# Revit family: Faucet-Symmons-Duro-Lavatory_Pop_Up_Drain
name_source: partatom
category: Plumbing Fixtures
revit_build: Autodesk Revit 2015 (Build: 20140606_1530(x64)
units: mm (PartAtom-declared; Revit-internal decimal feet)

## types (4) — shared parameters
Date Modified = January 30, 2015
Equipment Abbreviation = LF
Family Version = 1.0
Manufacturer = Symmons Industries, Inc.
Model Disclaimer = Contact Symmons Industries, Inc. For More Information
Product Documentation Link = http://www.symmons.com
Product Page URL = http://www.symmons.com
Product data url = https://bimobject.com
URL = http://www.symmons.com
z GPM GPM = 1.000 GPM

## per-type parameters (varying)
| type | Description | Gallons Per Minute | Model | Product Material | z GPM Number | z Type Finish | z Type Flow Restrictor | z Type GPM |
| 2.2 Flow Restrictor, Chrome | Lavatory Faucet with Pop-Up Drain, 2.2 Flow Rate Restrictor, Chrome | 2.200 GPM | SLS-3612 | Chrome - Symmons - Polished | 2.2 | 3 | 0 | 2.2 |
| 2.2 Flow Restrictor, Satin Nickel | Lavatory Faucet with Pop-Up Drain, 2.2 Flow Rate Restrictor, Satin Nickel | 2.200 GPM | SLS-3612-STN | Nickel - Symmons - Satin | 2.2 | 4 | 0 | 2.2 |
| 1.5 Flow Restrictor, Chrome | Lavatory Faucet with Pop-Up Drain, 1.5 Flow Rate Restrictor, Chrome | 1.500 GPM | SLS-3612-1.5 | Chrome - Symmons - Polished | 1.5 | 1 | 1 | 1.5 |
| 1.5 Flow Restrictor, Satin Nickel | Lavatory Faucet with Pop-Up Drain, 1.5 Flow Rate Restrictor, Satin Nickel | 1.500 GPM | SLS-3612-STN-1.5 | Nickel - Symmons - Satin | 1.5 | 2 | 1 | 1.5 |

## geometry (parser evidence)
native form markers: Blend x6, Sweep x5
no freeform markers — native parametric forms only
